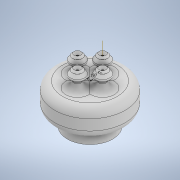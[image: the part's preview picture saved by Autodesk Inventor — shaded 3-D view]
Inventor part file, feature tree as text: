
AUTODESK INVENTOR PART (.ipt)
format: ipt  version: 2020 (Build 240168000, 168)  size: 358,400 bytes
history: native  units: in
note: dims shown in document units (in); Inventor stores cm internally (conversion verified against a paired STEP export)
features: sketch x3, revolve x2, fillet x2, other x1, pattern_circular x1
ambient origin geometry x8: Origin, YZ Plane, XZ Plane, XY Plane, X Axis, Y Axis, Z Axis, Center Point
bodies: Solid1 (feature_tree)
feature tree (9):
  revolve  "Revolution1"  [1 undecoded]
  sketch  "Sketch2"  dims[d2=0.2165in d3=0.0787in]
  other  "Work Axis1"
  revolve  "Revolution2"  [1 undecoded]
  pattern_circular  "Circular Pattern1"  [2 undecoded]
  fillet  "Fillet1"  Radius=0.1181in
  fillet  "Fillet2"  Radius=0.1181in
  sketch  "Sketch1"  dims[d0=0.1575in d1=0.2362in]
  sketch  "Sketch3"  dims[d4=0.1969in d5=0.1969in d6=0.1181in d7=0.1181in d9=90.0deg d10=0.1969in d11=0.0197in d12=0.1181in d13=0.0in d14=0.0787in d15=135.0deg d16=0.0787in d17=0.0492in d18=0.0394in d20=90.0deg d26=90.0deg d27=1.5748in d28=360.0deg d30=0.0787in d31=0.125in d32=0.0197in]
note: 4 required parameter values undecoded (feature->parameter linkage not recoverable at this tier; creation-order binding heuristic only, values carry confidence <= 0.55)